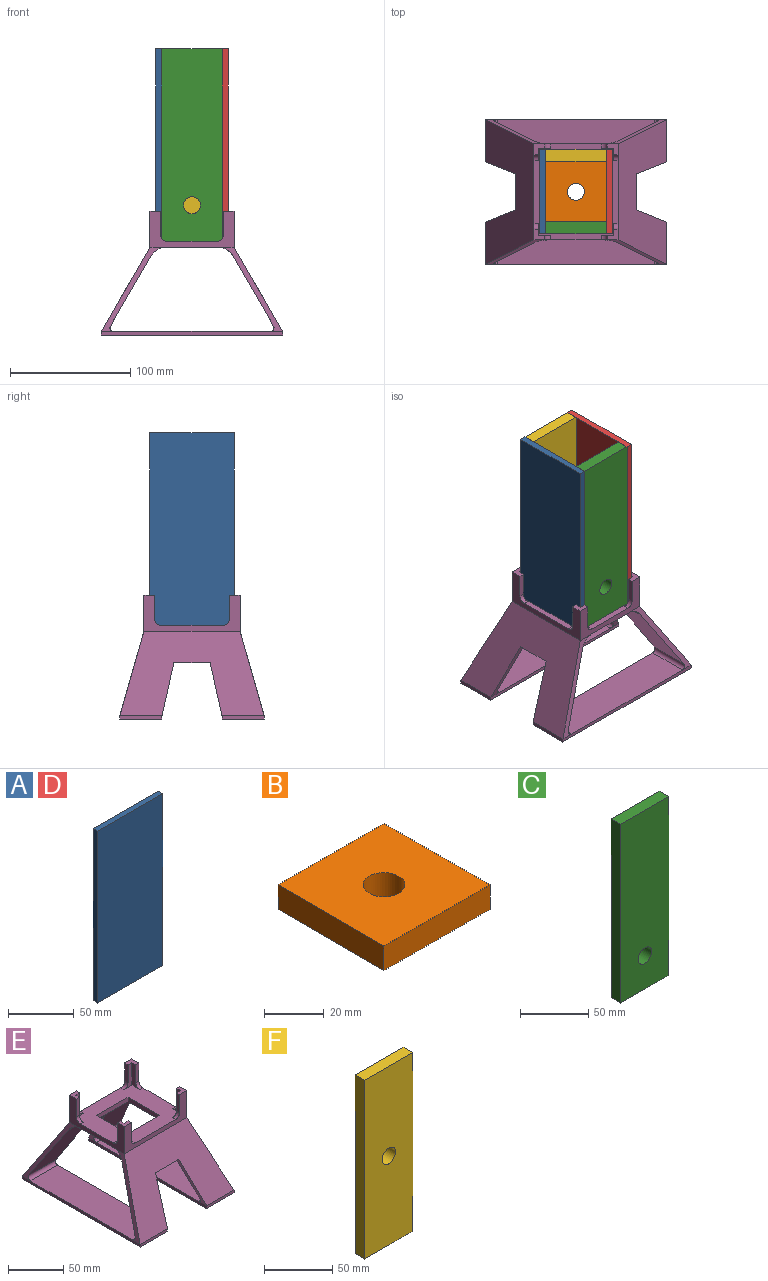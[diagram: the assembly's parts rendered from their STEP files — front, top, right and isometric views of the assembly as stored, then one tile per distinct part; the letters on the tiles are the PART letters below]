
ASSEMBLY  parts=6 mates=5
PART A: 6 faces, bbox 70x5x160 mm
  f0: plane 70x5mm, normal (0,0,1), area 350mm2, adj f1,f3,f4,f5
  f1: plane 160x5mm, normal (-1,0,0), area 800mm2, adj f0,f2,f4,f5
  f2: plane 70x5mm, normal (0,0,-1), area 350mm2, adj f1,f3,f4,f5
  f3: plane 160x5mm, normal (1,0,0), area 800mm2, adj f0,f2,f4,f5
  f4: plane 160x70mm, normal (0,-1,0), area 11200mm2, adj f0,f1,f2,f3
  f5: plane 160x70mm, normal (0,1,0), area 11200mm2, adj f0,f1,f2,f3
PART B: 7 faces, bbox 50x50x10 mm
  f0: plane 50x10mm, normal (0,1,0), area 500mm2, adj f1,f4,f5,f6
  f1: plane 50x10mm, normal (-1,0,0), area 500mm2, adj f0,f2,f5,f6
  f2: plane 50x10mm, normal (0,-1,0), area 500mm2, adj f1,f4,f5,f6
  f3: cylinder r=7mm len=14mm, axis (0,0,-1), area 439.8mm2, adj f5,f6
  f4: plane 50x10mm, normal (1,0,0), area 500mm2, adj f0,f2,f5,f6
  f5: plane 50x50mm, normal (0,0,1), area 2346.1mm2, adj f0,f1,f2,f3,f4
  f6: plane 50x50mm, normal (0,0,-1), area 2346.1mm2, adj f0,f1,f2,f3,f4
PART C: 7 faces, bbox 50x10x160 mm
  f0: plane 50x10mm, normal (0,0,1), area 500mm2, adj f1,f4,f5,f6
  f1: plane 160x10mm, normal (-1,0,0), area 1600mm2, adj f0,f2,f5,f6
  f2: plane 50x10mm, normal (0,0,-1), area 500mm2, adj f1,f4,f5,f6
  f3: cylinder r=7mm len=14mm, axis (0,1,0), area 439.8mm2, adj f5,f6
  f4: plane 160x10mm, normal (1,0,0), area 1600mm2, adj f0,f2,f5,f6
  f5: plane 160x50mm, normal (0,-1,0), area 7846.1mm2, adj f0,f1,f2,f3,f4
  f6: plane 160x50mm, normal (0,1,0), area 7846.1mm2, adj f0,f1,f2,f3,f4
PART D: same geometry as A
PART E: 70 faces, bbox 121.2x152x104.2 mm
  f0: plane 120x70mm, normal (0,0.87,0.5), area 6056.4mm2, adj f15,f39,f40,f41,f42,f43,f48,f55
  f1: plane 117.43x58mm, normal (0,-0.87,-0.5), area 4982.7mm2, adj f39,f40,f41,f42,f43,f45,f66,f69
  f2: plane 120x70mm, normal (0,-0.87,0.5), area 6056.4mm2, adj f13,f34,f35,f36,f37,f38,f50,f53
  f3: plane 117.43x58mm, normal (0,0.87,-0.5), area 4982.7mm2, adj f34,f35,f36,f37,f38,f44,f67,f68
  f4: plane 70x30mm, normal (1,0,0), area 810.7mm2, adj f5,f6,f7,f13,f14,f15,f26,f27
  f5: plane 80x42.68mm, normal (0,0,-1), area 1814.4mm2, adj f4,f16,f30,f31,f32,f33,f44,f45
  f6: plane 80x70mm, normal (0,0,1), area 3616mm2, adj f4,f8,f9,f11,f12,f13,f15,f16
  f7: plane 9x9mm, normal (0,0,1), area 56mm2, adj f4,f9,f11,f15,f25,f27
  f8: plane 25x10mm, normal (1,0,0), area 130.4mm2, adj f6,f10,f18,f29,f61
  f9: plane 25x10mm, normal (-1,0,0), area 130.4mm2, adj f6,f7,f11,f27,f59
  f10: plane 9x9mm, normal (0,0,1), area 56mm2, adj f8,f15,f16,f18,f24,f29
  f11: plane 25x10mm, normal (0,-1,0), area 130.4mm2, adj f6,f7,f9,f25,f65
  f12: plane 25x10mm, normal (0,1,0), area 130.4mm2, adj f6,f14,f19,f22,f63
  f13: plane 80x30mm, normal (0,-1,0), area 860.7mm2, adj f2,f4,f6,f14,f16,f21,f22,f23
  f14: plane 9x9mm, normal (0,0,1), area 56mm2, adj f4,f12,f13,f19,f22,f26
  f15: plane 80x30mm, normal (0,1,0), area 860.7mm2, adj f0,f4,f6,f7,f10,f16,f24,f25
  f16: plane 70x30mm, normal (-1,0,0), area 810.7mm2, adj f5,f6,f10,f13,f15,f21,f28,f29
  f17: plane 25x10mm, normal (1,0,0), area 130.4mm2, adj f6,f20,f21,f28,f60
  f18: plane 25x10mm, normal (0,-1,0), area 130.4mm2, adj f6,f8,f10,f24,f64
  f19: plane 25x10mm, normal (-1,0,0), area 130.4mm2, adj f6,f12,f14,f26,f58
  f20: plane 25x10mm, normal (0,1,0), area 130.4mm2, adj f6,f17,f21,f23,f62
  f21: plane 9x9mm, normal (0,0,1), area 56mm2, adj f13,f16,f17,f20,f23,f28
  f22: plane 20x4mm, normal (-1,0,0), area 80mm2, adj f12,f13,f14,f63
  f23: plane 20x4mm, normal (1,0,0), area 80mm2, adj f13,f20,f21,f62
  f24: plane 20x4mm, normal (1,0,0), area 80mm2, adj f10,f15,f18,f64
  f25: plane 20x4mm, normal (-1,0,0), area 80mm2, adj f7,f11,f15,f65
  f26: plane 20x4mm, normal (0,1,0), area 80mm2, adj f4,f14,f19,f58
  f27: plane 20x4mm, normal (0,-1,0), area 80mm2, adj f4,f7,f9,f59
  f28: plane 20x4mm, normal (0,1,0), area 80mm2, adj f16,f17,f21,f60
  f29: plane 20x4mm, normal (0,-1,0), area 80mm2, adj f8,f10,f16,f61
  f30: plane 40x5mm, normal (0,-1,0), area 200mm2, adj f5,f6,f31,f33
  f31: plane 40x5mm, normal (1,0,0), area 200mm2, adj f5,f6,f30,f32
  f32: plane 40x5mm, normal (0,1,0), area 200mm2, adj f5,f6,f31,f33
  f33: plane 40x5mm, normal (-1,0,0), area 200mm2, adj f5,f6,f30,f32
  f34: plane 30x5mm, normal (0,0,-1), area 150mm2, adj f2,f3,f35,f36
  f35: plane 44.24x30.7mm, normal (-0.97,0,-0.22), area 231.3mm2, adj f2,f3,f34,f54,f68
  f36: plane 44.24x30.7mm, normal (0.97,0,-0.22), area 231.3mm2, adj f2,f3,f34,f49,f67
  f37: plane 71.19x55.27mm, normal (0.96,0,0.27), area 382.6mm2, adj f2,f3,f4,f44,f56,f68
  f38: plane 71.17x55.25mm, normal (-0.96,0,0.27), area 381.4mm2, adj f2,f3,f16,f44,f47,f67
  f39: plane 44.24x30.7mm, normal (0.97,0,-0.22), area 231.3mm2, adj f0,f1,f41,f49,f66
  f40: plane 44.24x30.7mm, normal (-0.97,0,-0.22), area 231.3mm2, adj f0,f1,f41,f54,f69
  f41: plane 30x5mm, normal (0,0,-1), area 150mm2, adj f0,f1,f39,f40
  f42: plane 71.17x55.25mm, normal (0.96,0,0.27), area 381.6mm2, adj f0,f1,f4,f45,f56,f69
  f43: plane 71.19x55.27mm, normal (-0.96,0,0.27), area 381.5mm2, adj f0,f1,f16,f45,f47,f66
  f44: bspline ~92.71x12.99mm, area 1298.7mm2, adj f3,f5,f37,f38
  f45: bspline ~92.71x12.99mm, area 1298.7mm2, adj f1,f5,f42,f43
  f46: plane 130.44x35mm, normal (0,0,1), area 4565.3mm2, adj f47,f49,f66,f67
  f47: plane 150.83x3mm, normal (-1,0,0), area 452.5mm2, adj f38,f43,f46,f48,f50,f51
  f48: plane 35x3mm, normal (0,1,0), area 105mm2, adj f0,f47,f49,f51
  f49: plane 150.83x3mm, normal (1,0,0), area 452.5mm2, adj f36,f39,f46,f48,f50,f51
  f50: plane 35x3mm, normal (0,-1,0), area 105mm2, adj f2,f47,f49,f51
  f51: plane 150.83x35mm, normal (0,0,-1), area 5279mm2, adj f47,f48,f49,f50
  f52: plane 130.44x35mm, normal (0,0,1), area 4565.3mm2, adj f54,f56,f68,f69
  f53: plane 35x3mm, normal (0,-1,0), area 105mm2, adj f2,f54,f56,f57
  f54: plane 150.83x3mm, normal (-1,0,0), area 452.5mm2, adj f35,f40,f52,f53,f55,f57
  f55: plane 35x3mm, normal (0,1,0), area 105mm2, adj f0,f54,f56,f57
  f56: plane 150.83x3mm, normal (1,0,0), area 452.5mm2, adj f37,f42,f52,f53,f55,f57
  f57: plane 150.83x35mm, normal (0,0,-1), area 5279mm2, adj f53,f54,f55,f56
  f58: cylinder r=5mm len=5mm, axis (1,0,0), area 31.4mm2, adj f4,f6,f19,f26
  f59: cylinder r=5mm len=5mm, axis (-1,0,0), area 31.4mm2, adj f4,f6,f9,f27
  f60: cylinder r=5mm len=5mm, axis (1,0,0), area 31.4mm2, adj f6,f16,f17,f28
  f61: cylinder r=5mm len=5mm, axis (-1,0,0), area 31.4mm2, adj f6,f8,f16,f29
  f62: cylinder r=5mm len=5mm, axis (0,-1,0), area 31.4mm2, adj f6,f13,f20,f23
  f63: cylinder r=5mm len=5mm, axis (0,1,0), area 31.4mm2, adj f6,f12,f13,f22
  f64: cylinder r=5mm len=5mm, axis (0,-1,0), area 31.4mm2, adj f6,f15,f18,f24
  f65: cylinder r=5mm len=5mm, axis (0,1,0), area 31.4mm2, adj f6,f11,f15,f25
  f66: cylinder r=3mm len=36.03mm, axis (-1,0,0), area 219.1mm2, adj f1,f39,f43,f46
  f67: cylinder r=3mm len=36.03mm, axis (1,0,0), area 219.1mm2, adj f3,f36,f38,f46
  f68: cylinder r=3mm len=36.03mm, axis (1,0,0), area 219.1mm2, adj f3,f35,f37,f52
  f69: cylinder r=3mm len=36.03mm, axis (-1,0,0), area 219.1mm2, adj f1,f40,f42,f52
PART F: 7 faces, bbox 50x10x160 mm
  f0: plane 50x10mm, normal (0,0,1), area 500mm2, adj f1,f4,f5,f6
  f1: plane 160x10mm, normal (-1,0,0), area 1600mm2, adj f0,f2,f5,f6
  f2: plane 50x10mm, normal (0,0,-1), area 500mm2, adj f1,f4,f5,f6
  f3: cylinder r=7mm len=14mm, axis (0,1,0), area 439.8mm2, adj f5,f6
  f4: plane 160x10mm, normal (1,0,0), area 1600mm2, adj f0,f2,f5,f6
  f5: plane 160x50mm, normal (0,-1,0), area 7846.1mm2, adj f0,f1,f2,f3,f4
  f6: plane 160x50mm, normal (0,1,0), area 7846.1mm2, adj f0,f1,f2,f3,f4
PLACE A rot(axis=(0,0,1),90deg) t=(-30,-2.43,75)mm
PLACE B t=(0,0,-5)mm fixed
PLACE C t=(0,-25,75)mm
PLACE D rot(axis=(0,0,1),90deg) t=(25,-2.43,75)mm
PLACE E rot(axis=(0,0,1),90deg) t=(0,0,-5)mm
PLACE F t=(0,35,75)mm
MATE fastened F.f5 <-> B.f0  axis (0,-1,0) through (0,25,-5)mm
MATE fastened D.f5 <-> B.f4  axis (-1,0,0) through (25,0,-5)mm
MATE fastened E.f6 <-> B.f3  axis (0,0,1) through (0,0,-5)mm
MATE fastened C.f6 <-> B.f2  axis (0,1,0) through (0,-25,-5)mm
MATE fastened A.f4 <-> B.f1  axis (1,0,0) through (-25,0,-5)mm
